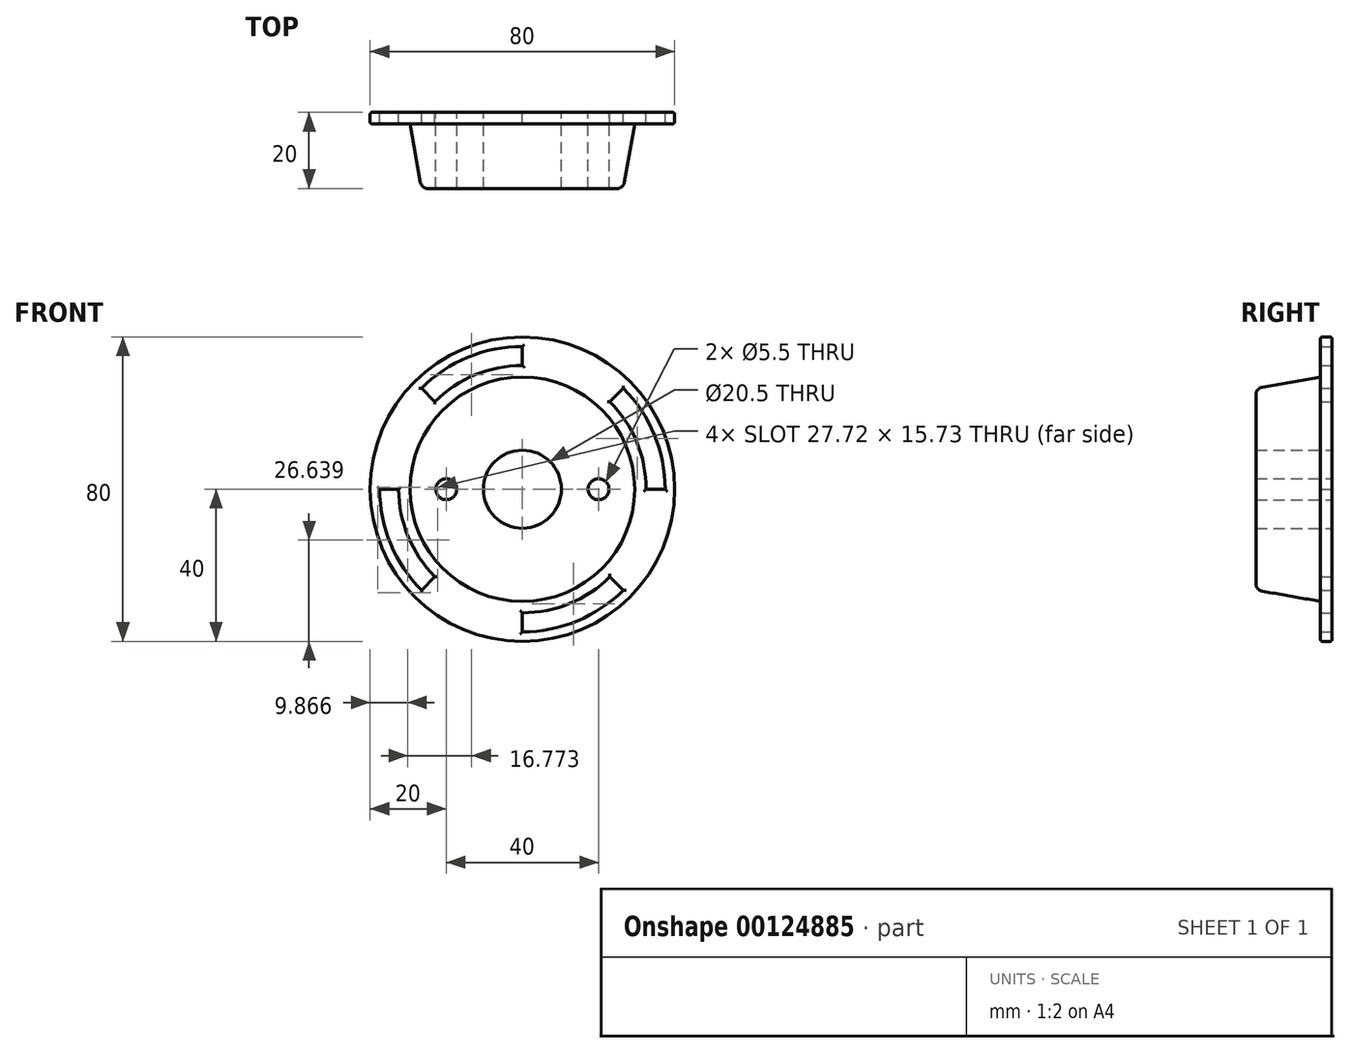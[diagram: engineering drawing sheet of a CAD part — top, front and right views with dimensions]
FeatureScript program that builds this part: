
annotation { "Feature Type Name" : "Feature", "Feature Type Description" : "" }
export const myFeature = defineFeature(function(context is Context, id is Id, definition is map)
    precondition{}
    {
        {
            var Q0;
            Q0=qCreatedBy(makeId("Front.planeOp"),FACE);
            var sketch = newSketch(context, id + "F0", { "sketchPlane" : qUnion([Q0])});
            skCircle(sketch, "E0", {"center": v(0, 0) * mm, "radius": 40 * mm});
            skCircle(sketch, "E1", {"center": v(0, 0) * mm, "radius": 29.5 * mm});
            skCircle(sketch, "E2", {"center": v(0, 0) * mm, "radius": 10.25 * mm});
            skCircle(sketch, "E3", {"center": v(0, 0) * mm, "radius": 37.5 * mm});
            skCircle(sketch, "E4", {"center": v(0, 0) * mm, "radius": 32.5 * mm});
            skLineSegment(sketch, "E5", {"start": v(0, 0) * mm, "end": v(0, 40) * mm});
            skLineSegment(sketch, "E6", {"start": v(0, 0) * mm, "end": v(40, 0) * mm});
            skLineSegment(sketch, "E7", {"start": v(0, 0) * mm, "end": v(0, -40) * mm});
            skLineSegment(sketch, "E8", {"start": v(0, 0) * mm, "end": v(-40, 0) * mm});
            skLineSegment(sketch, "E9", {"start": v(0, 0) * mm, "end": v(-28.28, 28.28) * mm});
            skLineSegment(sketch, "E10", {"start": v(0, 0) * mm, "end": v(28.28, 28.28) * mm});
            skLineSegment(sketch, "E11", {"start": v(0, 0) * mm, "end": v(28.28, -28.28) * mm});
            skLineSegment(sketch, "E12", {"start": v(0, 0) * mm, "end": v(-28.28, -28.28) * mm});
            skCircle(sketch, "E13", {"center": v(-20, 0) * mm, "radius": 2.75 * mm});
            skCircle(sketch, "E14.MirrorC", {"center": v(20, 0) * mm, "radius": 2.75 * mm});
            skSolve(sketch);
        }
        {
            var Q0;
            {var subQ0=sQuery(id+"F0.wireOp",EDGE,"E8");var subQ1=sQuery(id+"F0.wireOp",EDGE,"E1");var subQ2=makeQuery(id+"F0.imprint","INTERSECT",VERTEX,{"derivedFrom":[subQ1,subQ0]});Q0=makeQuery(id+"F0.imprint","IMPRINT",FACE,{"disambiguationData":[TD([[makeQuery(id+"F0.imprint","IMPRINT",EDGE,{"disambiguationData":[TD([[subQ2,-1.0]])],"derivedFrom":subQ1}),1.0]])]});}
            var Q1;
            {var subQ0=sQuery(id+"F0.wireOp",EDGE,"E9");var subQ1=sQuery(id+"F0.wireOp",EDGE,"E1");var subQ2=makeQuery(id+"F0.imprint","INTERSECT",VERTEX,{"derivedFrom":[subQ1,subQ0]});Q1=makeQuery(id+"F0.imprint","IMPRINT",FACE,{"disambiguationData":[TD([[makeQuery(id+"F0.imprint","IMPRINT",EDGE,{"disambiguationData":[TD([[subQ2,-1.0]])],"derivedFrom":subQ1}),1.0]])]});}
            var Q2;
            {var subQ0=sQuery(id+"F0.wireOp",EDGE,"E5");var subQ1=sQuery(id+"F0.wireOp",EDGE,"E1");var subQ2=makeQuery(id+"F0.imprint","INTERSECT",VERTEX,{"derivedFrom":[subQ1,subQ0]});Q2=makeQuery(id+"F0.imprint","IMPRINT",FACE,{"disambiguationData":[TD([[makeQuery(id+"F0.imprint","IMPRINT",EDGE,{"disambiguationData":[TD([[subQ2,-1.0]])],"derivedFrom":subQ1}),1.0]])]});}
            var Q3;
            {var subQ0=sQuery(id+"F0.wireOp",EDGE,"E10");var subQ1=sQuery(id+"F0.wireOp",EDGE,"E1");var subQ2=makeQuery(id+"F0.imprint","INTERSECT",VERTEX,{"derivedFrom":[subQ1,subQ0]});Q3=makeQuery(id+"F0.imprint","IMPRINT",FACE,{"disambiguationData":[TD([[makeQuery(id+"F0.imprint","IMPRINT",EDGE,{"disambiguationData":[TD([[subQ2,-1.0]])],"derivedFrom":subQ1}),1.0]])]});}
            var Q4;
            {var subQ0=sQuery(id+"F0.wireOp",EDGE,"E10");var subQ1=sQuery(id+"F0.wireOp",EDGE,"E1");var subQ2=makeQuery(id+"F0.imprint","INTERSECT",VERTEX,{"derivedFrom":[subQ1,subQ0]});Q4=makeQuery(id+"F0.imprint","IMPRINT",FACE,{"disambiguationData":[TD([[makeQuery(id+"F0.imprint","IMPRINT",EDGE,{"disambiguationData":[TD([[subQ2,1.0]])],"derivedFrom":subQ1}),1.0]])]});}
            var Q5;
            {var subQ0=sQuery(id+"F0.wireOp",EDGE,"E6");var subQ1=sQuery(id+"F0.wireOp",EDGE,"E1");var subQ2=makeQuery(id+"F0.imprint","INTERSECT",VERTEX,{"derivedFrom":[subQ1,subQ0]});Q5=makeQuery(id+"F0.imprint","IMPRINT",FACE,{"disambiguationData":[TD([[makeQuery(id+"F0.imprint","IMPRINT",EDGE,{"disambiguationData":[TD([[subQ2,1.0]])],"derivedFrom":subQ1}),1.0]])]});}
            var Q6;
            {var subQ0=sQuery(id+"F0.wireOp",EDGE,"E7");var subQ1=sQuery(id+"F0.wireOp",EDGE,"E1");var subQ2=makeQuery(id+"F0.imprint","INTERSECT",VERTEX,{"derivedFrom":[subQ1,subQ0]});Q6=makeQuery(id+"F0.imprint","IMPRINT",FACE,{"disambiguationData":[TD([[makeQuery(id+"F0.imprint","IMPRINT",EDGE,{"disambiguationData":[TD([[subQ2,-1.0]])],"derivedFrom":subQ1}),1.0]])]});}
            var Q7;
            {var subQ0=sQuery(id+"F0.wireOp",EDGE,"E12");var subQ1=sQuery(id+"F0.wireOp",EDGE,"E1");var subQ2=makeQuery(id+"F0.imprint","INTERSECT",VERTEX,{"derivedFrom":[subQ1,subQ0]});Q7=makeQuery(id+"F0.imprint","IMPRINT",FACE,{"disambiguationData":[TD([[makeQuery(id+"F0.imprint","IMPRINT",EDGE,{"disambiguationData":[TD([[subQ2,-1.0]])],"derivedFrom":subQ1}),1.0]])]});}
            extrude(context, id + "F1", {"entities" : qUnion([Q0, Q1, Q2, Q3, Q4, Q5, Q6, Q7]), "offsetDistance" : 25 * mm, "depth" : 20 * mm});
        }
        {
            var Q0;
            {var subQ0=sQuery(id+"F0.wireOp",EDGE,"E8");var subQ1=sQuery(id+"F0.wireOp",EDGE,"E1");var subQ2=makeQuery(id+"F0.imprint","INTERSECT",VERTEX,{"derivedFrom":[subQ1,subQ0]});Q0=makeQuery(id+"F0.imprint","IMPRINT",FACE,{"disambiguationData":[TD([[makeQuery(id+"F0.imprint","IMPRINT",EDGE,{"disambiguationData":[TD([[subQ2,-1.0]])],"derivedFrom":subQ1}),-1.0]])]});}
            var Q1;
            {var subQ0=sQuery(id+"F0.wireOp",EDGE,"E8");var subQ1=sQuery(id+"F0.wireOp",EDGE,"E0");var subQ2=makeQuery(id+"F0.imprint","INTERSECT",VERTEX,{"derivedFrom":[subQ1,subQ0]});Q1=makeQuery(id+"F0.imprint","IMPRINT",FACE,{"disambiguationData":[TD([[makeQuery(id+"F0.imprint","IMPRINT",EDGE,{"disambiguationData":[TD([[subQ2,-1.0]])],"derivedFrom":subQ1}),1.0]])]});}
            var Q2;
            {var subQ0=sQuery(id+"F0.wireOp",EDGE,"E8");var subQ1=sQuery(id+"F0.wireOp",EDGE,"E0");var subQ2=makeQuery(id+"F0.imprint","INTERSECT",VERTEX,{"derivedFrom":[subQ1,subQ0]});Q2=makeQuery(id+"F0.imprint","IMPRINT",FACE,{"disambiguationData":[TD([[makeQuery(id+"F0.imprint","IMPRINT",EDGE,{"disambiguationData":[TD([[subQ2,1.0]])],"derivedFrom":subQ1}),1.0]])]});}
            var Q3;
            {var subQ0=sQuery(id+"F0.wireOp",EDGE,"E9");var subQ1=sQuery(id+"F0.wireOp",EDGE,"E3");var subQ2=makeQuery(id+"F0.imprint","INTERSECT",VERTEX,{"derivedFrom":[subQ1,subQ0]});Q3=makeQuery(id+"F0.imprint","IMPRINT",FACE,{"disambiguationData":[TD([[makeQuery(id+"F0.imprint","IMPRINT",EDGE,{"disambiguationData":[TD([[subQ2,-1.0]])],"derivedFrom":subQ1}),1.0]])]});}
            var Q4;
            {var subQ0=sQuery(id+"F0.wireOp",EDGE,"E9");var subQ1=sQuery(id+"F0.wireOp",EDGE,"E1");var subQ2=makeQuery(id+"F0.imprint","INTERSECT",VERTEX,{"derivedFrom":[subQ1,subQ0]});Q4=makeQuery(id+"F0.imprint","IMPRINT",FACE,{"disambiguationData":[TD([[makeQuery(id+"F0.imprint","IMPRINT",EDGE,{"disambiguationData":[TD([[subQ2,-1.0]])],"derivedFrom":subQ1}),-1.0]])]});}
            var Q5;
            {var subQ0=sQuery(id+"F0.wireOp",EDGE,"E12");var subQ1=sQuery(id+"F0.wireOp",EDGE,"E1");var subQ2=makeQuery(id+"F0.imprint","INTERSECT",VERTEX,{"derivedFrom":[subQ1,subQ0]});Q5=makeQuery(id+"F0.imprint","IMPRINT",FACE,{"disambiguationData":[TD([[makeQuery(id+"F0.imprint","IMPRINT",EDGE,{"disambiguationData":[TD([[subQ2,-1.0]])],"derivedFrom":subQ1}),-1.0]])]});}
            var Q6;
            {var subQ0=sQuery(id+"F0.wireOp",EDGE,"E12");var subQ1=sQuery(id+"F0.wireOp",EDGE,"E3");var subQ2=makeQuery(id+"F0.imprint","INTERSECT",VERTEX,{"derivedFrom":[subQ1,subQ0]});Q6=makeQuery(id+"F0.imprint","IMPRINT",FACE,{"disambiguationData":[TD([[makeQuery(id+"F0.imprint","IMPRINT",EDGE,{"disambiguationData":[TD([[subQ2,-1.0]])],"derivedFrom":subQ1}),1.0]])]});}
            var Q7;
            {var subQ0=sQuery(id+"F0.wireOp",EDGE,"E7");var subQ1=sQuery(id+"F0.wireOp",EDGE,"E0");var subQ2=makeQuery(id+"F0.imprint","INTERSECT",VERTEX,{"derivedFrom":[subQ1,subQ0]});Q7=makeQuery(id+"F0.imprint","IMPRINT",FACE,{"disambiguationData":[TD([[makeQuery(id+"F0.imprint","IMPRINT",EDGE,{"disambiguationData":[TD([[subQ2,1.0]])],"derivedFrom":subQ1}),1.0]])]});}
            var Q8;
            {var subQ0=sQuery(id+"F0.wireOp",EDGE,"E5");var subQ1=sQuery(id+"F0.wireOp",EDGE,"E1");var subQ2=makeQuery(id+"F0.imprint","INTERSECT",VERTEX,{"derivedFrom":[subQ1,subQ0]});Q8=makeQuery(id+"F0.imprint","IMPRINT",FACE,{"disambiguationData":[TD([[makeQuery(id+"F0.imprint","IMPRINT",EDGE,{"disambiguationData":[TD([[subQ2,-1.0]])],"derivedFrom":subQ1}),-1.0]])]});}
            var Q9;
            {var subQ0=sQuery(id+"F0.wireOp",EDGE,"E5");var subQ1=sQuery(id+"F0.wireOp",EDGE,"E0");var subQ2=makeQuery(id+"F0.imprint","INTERSECT",VERTEX,{"derivedFrom":[subQ1,subQ0]});Q9=makeQuery(id+"F0.imprint","IMPRINT",FACE,{"disambiguationData":[TD([[makeQuery(id+"F0.imprint","IMPRINT",EDGE,{"disambiguationData":[TD([[subQ2,-1.0]])],"derivedFrom":subQ1}),1.0]])]});}
            var Q10;
            {var subQ0=sQuery(id+"F0.wireOp",EDGE,"E5");var subQ1=sQuery(id+"F0.wireOp",EDGE,"E0");var subQ2=makeQuery(id+"F0.imprint","INTERSECT",VERTEX,{"derivedFrom":[subQ1,subQ0]});Q10=makeQuery(id+"F0.imprint","IMPRINT",FACE,{"disambiguationData":[TD([[makeQuery(id+"F0.imprint","IMPRINT",EDGE,{"disambiguationData":[TD([[subQ2,1.0]])],"derivedFrom":subQ1}),1.0]])]});}
            var Q11;
            {var subQ0=sQuery(id+"F0.wireOp",EDGE,"E10");var subQ1=sQuery(id+"F0.wireOp",EDGE,"E3");var subQ2=makeQuery(id+"F0.imprint","INTERSECT",VERTEX,{"derivedFrom":[subQ1,subQ0]});Q11=makeQuery(id+"F0.imprint","IMPRINT",FACE,{"disambiguationData":[TD([[makeQuery(id+"F0.imprint","IMPRINT",EDGE,{"disambiguationData":[TD([[subQ2,-1.0]])],"derivedFrom":subQ1}),1.0]])]});}
            var Q12;
            {var subQ0=sQuery(id+"F0.wireOp",EDGE,"E10");var subQ1=sQuery(id+"F0.wireOp",EDGE,"E1");var subQ2=makeQuery(id+"F0.imprint","INTERSECT",VERTEX,{"derivedFrom":[subQ1,subQ0]});Q12=makeQuery(id+"F0.imprint","IMPRINT",FACE,{"disambiguationData":[TD([[makeQuery(id+"F0.imprint","IMPRINT",EDGE,{"disambiguationData":[TD([[subQ2,-1.0]])],"derivedFrom":subQ1}),-1.0]])]});}
            var Q13;
            {var subQ0=sQuery(id+"F0.wireOp",EDGE,"E6");var subQ1=sQuery(id+"F0.wireOp",EDGE,"E0");var subQ2=makeQuery(id+"F0.imprint","INTERSECT",VERTEX,{"derivedFrom":[subQ1,subQ0]});Q13=makeQuery(id+"F0.imprint","IMPRINT",FACE,{"disambiguationData":[TD([[makeQuery(id+"F0.imprint","IMPRINT",EDGE,{"disambiguationData":[TD([[subQ2,-1.0]])],"derivedFrom":subQ1}),1.0]])]});}
            var Q14;
            {var subQ0=sQuery(id+"F0.wireOp",EDGE,"E10");var subQ1=sQuery(id+"F0.wireOp",EDGE,"E1");var subQ2=makeQuery(id+"F0.imprint","INTERSECT",VERTEX,{"derivedFrom":[subQ1,subQ0]});Q14=makeQuery(id+"F0.imprint","IMPRINT",FACE,{"disambiguationData":[TD([[makeQuery(id+"F0.imprint","IMPRINT",EDGE,{"disambiguationData":[TD([[subQ2,1.0]])],"derivedFrom":subQ1}),-1.0]])]});}
            var Q15;
            {var subQ0=sQuery(id+"F0.wireOp",EDGE,"E6");var subQ1=sQuery(id+"F0.wireOp",EDGE,"E0");var subQ2=makeQuery(id+"F0.imprint","INTERSECT",VERTEX,{"derivedFrom":[subQ1,subQ0]});Q15=makeQuery(id+"F0.imprint","IMPRINT",FACE,{"disambiguationData":[TD([[makeQuery(id+"F0.imprint","IMPRINT",EDGE,{"disambiguationData":[TD([[subQ2,1.0]])],"derivedFrom":subQ1}),1.0]])]});}
            var Q16;
            {var subQ0=sQuery(id+"F0.wireOp",EDGE,"E6");var subQ1=sQuery(id+"F0.wireOp",EDGE,"E3");var subQ2=makeQuery(id+"F0.imprint","INTERSECT",VERTEX,{"derivedFrom":[subQ1,subQ0]});Q16=makeQuery(id+"F0.imprint","IMPRINT",FACE,{"disambiguationData":[TD([[makeQuery(id+"F0.imprint","IMPRINT",EDGE,{"disambiguationData":[TD([[subQ2,1.0]])],"derivedFrom":subQ1}),1.0]])]});}
            var Q17;
            {var subQ0=sQuery(id+"F0.wireOp",EDGE,"E6");var subQ1=sQuery(id+"F0.wireOp",EDGE,"E1");var subQ2=makeQuery(id+"F0.imprint","INTERSECT",VERTEX,{"derivedFrom":[subQ1,subQ0]});Q17=makeQuery(id+"F0.imprint","IMPRINT",FACE,{"disambiguationData":[TD([[makeQuery(id+"F0.imprint","IMPRINT",EDGE,{"disambiguationData":[TD([[subQ2,1.0]])],"derivedFrom":subQ1}),-1.0]])]});}
            var Q18;
            {var subQ0=sQuery(id+"F0.wireOp",EDGE,"E7");var subQ1=sQuery(id+"F0.wireOp",EDGE,"E1");var subQ2=makeQuery(id+"F0.imprint","INTERSECT",VERTEX,{"derivedFrom":[subQ1,subQ0]});Q18=makeQuery(id+"F0.imprint","IMPRINT",FACE,{"disambiguationData":[TD([[makeQuery(id+"F0.imprint","IMPRINT",EDGE,{"disambiguationData":[TD([[subQ2,-1.0]])],"derivedFrom":subQ1}),-1.0]])]});}
            var Q19;
            {var subQ0=sQuery(id+"F0.wireOp",EDGE,"E7");var subQ1=sQuery(id+"F0.wireOp",EDGE,"E0");var subQ2=makeQuery(id+"F0.imprint","INTERSECT",VERTEX,{"derivedFrom":[subQ1,subQ0]});Q19=makeQuery(id+"F0.imprint","IMPRINT",FACE,{"disambiguationData":[TD([[makeQuery(id+"F0.imprint","IMPRINT",EDGE,{"disambiguationData":[TD([[subQ2,-1.0]])],"derivedFrom":subQ1}),1.0]])]});}
            extrude(context, id + "F2", {"entities" : qUnion([Q0, Q1, Q2, Q3, Q4, Q5, Q6, Q7, Q8, Q9, Q10, Q11, Q12, Q13, Q14, Q15, Q16, Q17, Q18, Q19]), "operationType" : NewBodyOperationType.ADD, "depth" : 3 * mm});
        }
        {
            var Q0;
            Q0=makeQuery(id+"F1.opExtrude","CAP_EDGE",EDGE,{"disambiguationData":[OSD([sQuery(id+"F0.wireOp",EDGE,"E1")])],"isStart":false});
            chamfer(context, id + "F3", {"entities" : qUnion([Q0]), "chamferType" : ChamferType.TWO_OFFSETS, "width1" : 3 * mm, "oppositeDirection" : false, "width2" : 17 * mm, "tangentPropagation" : true});
        }
        {
            var Q0;
            {var subQ0=sQuery(id+"F0.wireOp",EDGE,"E1");Q0=makeQuery(id+"F3.opChamfer","BLEND_EDGE",EDGE,{"blendedFrom":[makeQuery(id+"F1.opExtrude","CAP_EDGE",EDGE,{"disambiguationData":[OSD([subQ0])],"isStart":false}),makeQuery(id+"F1.opExtrude","CAP_FACE",FACE,{"disambiguationData":[OSD([subQ0,sQuery(id+"F0.wireOp",EDGE,"E2")])],"isStart":false})],"blendedInto":[makeQuery(id+"F1.opExtrude","CAP_FACE",FACE,{"disambiguationData":[OSD([subQ0,sQuery(id+"F0.wireOp",EDGE,"E2")])],"isStart":false})]});}
            fillet(context, id + "F4", {"entities" : qUnion([Q0]), "radius" : 2 * mm, "tangentPropagation" : true, "allowEdgeOverflow" : false});
        }
        {
            var Q0;
            Q0=makeQuery(id+"F2.opExtrude","CAP_EDGE",EDGE,{"disambiguationData":[OSD([sQuery(id+"F0.wireOp",EDGE,"E8")])],"isStart":false});
            var Q1;
            {var subQ0=sQuery(id+"F0.wireOp",EDGE,"E3");Q1=makeQuery(id+"F2.opExtrude","CAP_EDGE",EDGE,{"disambiguationData":[OSD([subQ0]),TDD([makeQuery(id+"F0.imprint","IMPRINT",EDGE,{"disambiguationData":[TD([[makeQuery(id+"F0.imprint","INTERSECT",VERTEX,{"derivedFrom":[subQ0,sQuery(id+"F0.wireOp",EDGE,"E8")]}),-1.0]])],"derivedFrom":subQ0})])],"isStart":false});}
            var Q2;
            {var subQ0=sQuery(id+"F0.wireOp",EDGE,"E4");Q2=makeQuery(id+"F2.opExtrude","CAP_EDGE",EDGE,{"disambiguationData":[OSD([subQ0]),TDD([makeQuery(id+"F0.imprint","IMPRINT",EDGE,{"disambiguationData":[TD([[makeQuery(id+"F0.imprint","INTERSECT",VERTEX,{"derivedFrom":[subQ0,sQuery(id+"F0.wireOp",EDGE,"E8")]}),-1.0]])],"derivedFrom":subQ0})])],"isStart":false});}
            var Q3;
            Q3=makeQuery(id+"F2.opExtrude","CAP_EDGE",EDGE,{"disambiguationData":[OSD([sQuery(id+"F0.wireOp",EDGE,"E12")])],"isStart":false});
            var Q4;
            {var subQ0=sQuery(id+"F0.wireOp",EDGE,"E4");Q4=makeQuery(id+"F2.opExtrude","CAP_EDGE",EDGE,{"disambiguationData":[OSD([subQ0]),TDD([makeQuery(id+"F0.imprint","IMPRINT",EDGE,{"disambiguationData":[TD([[makeQuery(id+"F0.imprint","INTERSECT",VERTEX,{"derivedFrom":[subQ0,sQuery(id+"F0.wireOp",EDGE,"E7")]}),-1.0]])],"derivedFrom":subQ0})])],"isStart":false});}
            var Q5;
            {var subQ0=sQuery(id+"F0.wireOp",EDGE,"E3");Q5=makeQuery(id+"F2.opExtrude","CAP_EDGE",EDGE,{"disambiguationData":[OSD([subQ0]),TDD([makeQuery(id+"F0.imprint","IMPRINT",EDGE,{"disambiguationData":[TD([[makeQuery(id+"F0.imprint","INTERSECT",VERTEX,{"derivedFrom":[subQ0,sQuery(id+"F0.wireOp",EDGE,"E7")]}),-1.0]])],"derivedFrom":subQ0})])],"isStart":false});}
            var Q6;
            Q6=makeQuery(id+"F2.opExtrude","CAP_EDGE",EDGE,{"disambiguationData":[OSD([sQuery(id+"F0.wireOp",EDGE,"E7")])],"isStart":false});
            var Q7;
            Q7=makeQuery(id+"F2.opExtrude","CAP_EDGE",EDGE,{"disambiguationData":[OSD([sQuery(id+"F0.wireOp",EDGE,"E11")])],"isStart":false});
            var Q8;
            Q8=makeQuery(id+"F2.opExtrude","CAP_EDGE",EDGE,{"disambiguationData":[OSD([sQuery(id+"F0.wireOp",EDGE,"E6")])],"isStart":false});
            var Q9;
            {var subQ0=sQuery(id+"F0.wireOp",EDGE,"E4");Q9=makeQuery(id+"F2.opExtrude","CAP_EDGE",EDGE,{"disambiguationData":[OSD([subQ0]),TDD([makeQuery(id+"F0.imprint","IMPRINT",EDGE,{"disambiguationData":[TD([[makeQuery(id+"F0.imprint","INTERSECT",VERTEX,{"derivedFrom":[subQ0,sQuery(id+"F0.wireOp",EDGE,"E10")]}),1.0]])],"derivedFrom":subQ0})])],"isStart":false});}
            var Q10;
            {var subQ0=sQuery(id+"F0.wireOp",EDGE,"E3");Q10=makeQuery(id+"F2.opExtrude","CAP_EDGE",EDGE,{"disambiguationData":[OSD([subQ0]),TDD([makeQuery(id+"F0.imprint","IMPRINT",EDGE,{"disambiguationData":[TD([[makeQuery(id+"F0.imprint","INTERSECT",VERTEX,{"derivedFrom":[subQ0,sQuery(id+"F0.wireOp",EDGE,"E10")]}),1.0]])],"derivedFrom":subQ0})])],"isStart":false});}
            var Q11;
            Q11=makeQuery(id+"F2.opExtrude","CAP_EDGE",EDGE,{"disambiguationData":[OSD([sQuery(id+"F0.wireOp",EDGE,"E10")])],"isStart":false});
            var Q12;
            Q12=makeQuery(id+"F2.opExtrude","CAP_EDGE",EDGE,{"disambiguationData":[OSD([sQuery(id+"F0.wireOp",EDGE,"E5")])],"isStart":false});
            var Q13;
            Q13=makeQuery(id+"F2.opExtrude","CAP_EDGE",EDGE,{"disambiguationData":[OSD([sQuery(id+"F0.wireOp",EDGE,"E9")])],"isStart":false});
            var Q14;
            {var subQ0=sQuery(id+"F0.wireOp",EDGE,"E3");Q14=makeQuery(id+"F2.opExtrude","CAP_EDGE",EDGE,{"disambiguationData":[OSD([subQ0]),TDD([makeQuery(id+"F0.imprint","IMPRINT",EDGE,{"disambiguationData":[TD([[makeQuery(id+"F0.imprint","INTERSECT",VERTEX,{"derivedFrom":[subQ0,sQuery(id+"F0.wireOp",EDGE,"E5")]}),-1.0]])],"derivedFrom":subQ0})])],"isStart":false});}
            var Q15;
            {var subQ0=sQuery(id+"F0.wireOp",EDGE,"E4");Q15=makeQuery(id+"F2.opExtrude","CAP_EDGE",EDGE,{"disambiguationData":[OSD([subQ0]),TDD([makeQuery(id+"F0.imprint","IMPRINT",EDGE,{"disambiguationData":[TD([[makeQuery(id+"F0.imprint","INTERSECT",VERTEX,{"derivedFrom":[subQ0,sQuery(id+"F0.wireOp",EDGE,"E5")]}),-1.0]])],"derivedFrom":subQ0})])],"isStart":false});}
            var Q16;
            {var subQ0=sQuery(id+"F0.wireOp",EDGE,"E4");Q16=makeQuery(id+"F2.opExtrude","CAP_EDGE",EDGE,{"disambiguationData":[OSD([subQ0]),TDD([makeQuery(id+"F0.imprint","IMPRINT",EDGE,{"disambiguationData":[TD([[makeQuery(id+"F0.imprint","INTERSECT",VERTEX,{"derivedFrom":[subQ0,sQuery(id+"F0.wireOp",EDGE,"E7")]}),-1.0]])],"derivedFrom":subQ0})])],"isStart":true});}
            var Q17;
            Q17=makeQuery(id+"F2.opExtrude","CAP_EDGE",EDGE,{"disambiguationData":[OSD([sQuery(id+"F0.wireOp",EDGE,"E7")])],"isStart":true});
            var Q18;
            {var subQ0=sQuery(id+"F0.wireOp",EDGE,"E3");Q18=makeQuery(id+"F2.opExtrude","CAP_EDGE",EDGE,{"disambiguationData":[OSD([subQ0]),TDD([makeQuery(id+"F0.imprint","IMPRINT",EDGE,{"disambiguationData":[TD([[makeQuery(id+"F0.imprint","INTERSECT",VERTEX,{"derivedFrom":[subQ0,sQuery(id+"F0.wireOp",EDGE,"E7")]}),-1.0]])],"derivedFrom":subQ0})])],"isStart":true});}
            var Q19;
            Q19=makeQuery(id+"F2.opExtrude","CAP_EDGE",EDGE,{"disambiguationData":[OSD([sQuery(id+"F0.wireOp",EDGE,"E11")])],"isStart":true});
            var Q20;
            Q20=makeQuery(id+"F2.opExtrude","CAP_EDGE",EDGE,{"disambiguationData":[OSD([sQuery(id+"F0.wireOp",EDGE,"E6")])],"isStart":true});
            var Q21;
            {var subQ0=sQuery(id+"F0.wireOp",EDGE,"E4");Q21=makeQuery(id+"F2.opExtrude","CAP_EDGE",EDGE,{"disambiguationData":[OSD([subQ0]),TDD([makeQuery(id+"F0.imprint","IMPRINT",EDGE,{"disambiguationData":[TD([[makeQuery(id+"F0.imprint","INTERSECT",VERTEX,{"derivedFrom":[subQ0,sQuery(id+"F0.wireOp",EDGE,"E10")]}),1.0]])],"derivedFrom":subQ0})])],"isStart":true});}
            var Q22;
            {var subQ0=sQuery(id+"F0.wireOp",EDGE,"E3");Q22=makeQuery(id+"F2.opExtrude","CAP_EDGE",EDGE,{"disambiguationData":[OSD([subQ0]),TDD([makeQuery(id+"F0.imprint","IMPRINT",EDGE,{"disambiguationData":[TD([[makeQuery(id+"F0.imprint","INTERSECT",VERTEX,{"derivedFrom":[subQ0,sQuery(id+"F0.wireOp",EDGE,"E10")]}),1.0]])],"derivedFrom":subQ0})])],"isStart":true});}
            var Q23;
            Q23=makeQuery(id+"F2.opExtrude","CAP_EDGE",EDGE,{"disambiguationData":[OSD([sQuery(id+"F0.wireOp",EDGE,"E10")])],"isStart":true});
            var Q24;
            Q24=makeQuery(id+"F2.opExtrude","CAP_EDGE",EDGE,{"disambiguationData":[OSD([sQuery(id+"F0.wireOp",EDGE,"E5")])],"isStart":true});
            var Q25;
            Q25=makeQuery(id+"F2.opExtrude","CAP_EDGE",EDGE,{"disambiguationData":[OSD([sQuery(id+"F0.wireOp",EDGE,"E9")])],"isStart":true});
            var Q26;
            {var subQ0=sQuery(id+"F0.wireOp",EDGE,"E3");Q26=makeQuery(id+"F2.opExtrude","CAP_EDGE",EDGE,{"disambiguationData":[OSD([subQ0]),TDD([makeQuery(id+"F0.imprint","IMPRINT",EDGE,{"disambiguationData":[TD([[makeQuery(id+"F0.imprint","INTERSECT",VERTEX,{"derivedFrom":[subQ0,sQuery(id+"F0.wireOp",EDGE,"E5")]}),-1.0]])],"derivedFrom":subQ0})])],"isStart":true});}
            var Q27;
            {var subQ0=sQuery(id+"F0.wireOp",EDGE,"E4");Q27=makeQuery(id+"F2.opExtrude","CAP_EDGE",EDGE,{"disambiguationData":[OSD([subQ0]),TDD([makeQuery(id+"F0.imprint","IMPRINT",EDGE,{"disambiguationData":[TD([[makeQuery(id+"F0.imprint","INTERSECT",VERTEX,{"derivedFrom":[subQ0,sQuery(id+"F0.wireOp",EDGE,"E5")]}),-1.0]])],"derivedFrom":subQ0})])],"isStart":true});}
            var Q28;
            Q28=makeQuery(id+"F2.opExtrude","CAP_EDGE",EDGE,{"disambiguationData":[OSD([sQuery(id+"F0.wireOp",EDGE,"E8")])],"isStart":true});
            var Q29;
            {var subQ0=sQuery(id+"F0.wireOp",EDGE,"E4");Q29=makeQuery(id+"F2.opExtrude","CAP_EDGE",EDGE,{"disambiguationData":[OSD([subQ0]),TDD([makeQuery(id+"F0.imprint","IMPRINT",EDGE,{"disambiguationData":[TD([[makeQuery(id+"F0.imprint","INTERSECT",VERTEX,{"derivedFrom":[subQ0,sQuery(id+"F0.wireOp",EDGE,"E8")]}),-1.0]])],"derivedFrom":subQ0})])],"isStart":true});}
            var Q30;
            {var subQ0=sQuery(id+"F0.wireOp",EDGE,"E3");Q30=makeQuery(id+"F2.opExtrude","CAP_EDGE",EDGE,{"disambiguationData":[OSD([subQ0]),TDD([makeQuery(id+"F0.imprint","IMPRINT",EDGE,{"disambiguationData":[TD([[makeQuery(id+"F0.imprint","INTERSECT",VERTEX,{"derivedFrom":[subQ0,sQuery(id+"F0.wireOp",EDGE,"E8")]}),-1.0]])],"derivedFrom":subQ0})])],"isStart":true});}
            var Q31;
            Q31=makeQuery(id+"F2.opExtrude","CAP_EDGE",EDGE,{"disambiguationData":[OSD([sQuery(id+"F0.wireOp",EDGE,"E12")])],"isStart":true});
            var Q32;
            Q32=makeQuery(id+"F2.opExtrude","CAP_EDGE",EDGE,{"disambiguationData":[OSD([sQuery(id+"F0.wireOp",EDGE,"E0")])],"isStart":false});
            var Q33;
            Q33=makeQuery(id+"F2.opExtrude","CAP_EDGE",EDGE,{"disambiguationData":[OSD([sQuery(id+"F0.wireOp",EDGE,"E0")])],"isStart":true});
            fillet(context, id + "F5", {"entities" : qUnion([Q0, Q1, Q2, Q3, Q4, Q5, Q6, Q7, Q8, Q9, Q10, Q11, Q12, Q13, Q14, Q15, Q16, Q17, Q18, Q19, Q20, Q21, Q22, Q23, Q24, Q25, Q26, Q27, Q28, Q29, Q30, Q31, Q32, Q33]), "radius" : 0.5 * mm, "tangentPropagation" : true, "allowEdgeOverflow" : false});
        }
    });
